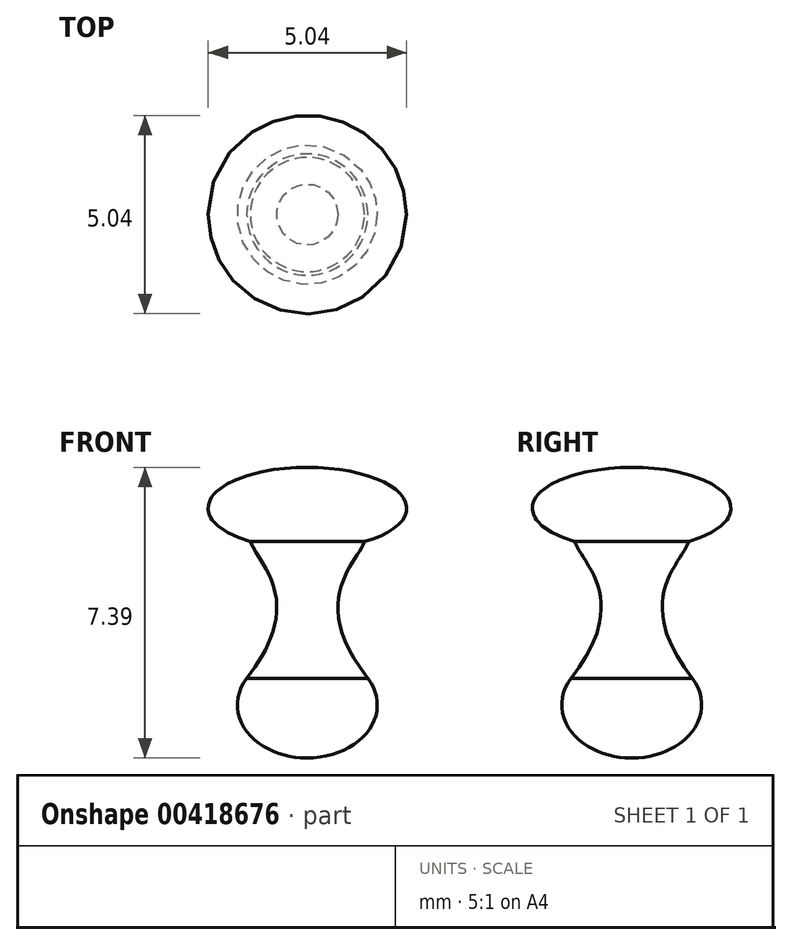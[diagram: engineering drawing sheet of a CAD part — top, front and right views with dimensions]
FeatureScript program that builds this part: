
annotation { "Feature Type Name" : "Feature", "Feature Type Description" : "" }
export const myFeature = defineFeature(function(context is Context, id is Id, definition is map)
    precondition{}
    {
        {
            var Q0;
            Q0=qCreatedBy(makeId("Front.planeOp"),FACE);
            var sketch = newSketch(context, id + "F0", { "sketchPlane" : qUnion([Q0])});
            skEllipse(sketch, "E0", {"center": v(0, 5) * mm, "majorRadius": 2.52 * mm, "minorRadius": 1.04 * mm, "majorAxis": v(-1, 0)});
            skEllipse(sketch, "E1", {"center": v(0, 0) * mm, "majorRadius": 1.78 * mm, "minorRadius": 1.35 * mm, "majorAxis": v(1, 0)});
            skLineSegment(sketch, "E2", {"start": v(0, 6.04) * mm, "end": v(0, 3.96) * mm});
            skLineSegment(sketch, "E3", {"start": v(0, 3.96) * mm, "end": v(0, 1.35) * mm});
            skLineSegment(sketch, "E4", {"start": v(0, 1.35) * mm, "end": v(0, -1.35) * mm});
            skFitSpline(sketch, "E5", {"points": [v(1.45, 4.15) * mm, v(1.54, 0.67) * mm], "startDerivative": vector(-0.67, -1.76) * mm, "endDerivative": vector(4.62, -5.94) * mm});
            skSolve(sketch);
        }
        {
            var Q0;
            {var subQ0=sQuery(id+"F0.wireOp",EDGE,"E2");Q0=makeQuery(id+"F0.imprint","IMPRINT",FACE,{"disambiguationData":[TD([[makeQuery(id+"F0.imprint","IMPRINT",EDGE,{"derivedFrom":subQ0}),1.0]])]});}
            var Q1;
            {var subQ0=sQuery(id+"F0.wireOp",EDGE,"E3");Q1=makeQuery(id+"F0.imprint","IMPRINT",FACE,{"disambiguationData":[TD([[makeQuery(id+"F0.imprint","IMPRINT",EDGE,{"derivedFrom":subQ0}),1.0]])]});}
            var Q2;
            {var subQ0=sQuery(id+"F0.wireOp",EDGE,"E4");Q2=makeQuery(id+"F0.imprint","IMPRINT",FACE,{"disambiguationData":[TD([[makeQuery(id+"F0.imprint","IMPRINT",EDGE,{"derivedFrom":subQ0}),1.0]])]});}
            var Q3;
            Q3=sQuery(id+"F0.wireOp",EDGE,"E3");
            revolve(context, id + "F1", {"surfaceOperationType" : NewSurfaceOperationType.NEW, "entities" : qUnion([Q0, Q1, Q2]), "axis" : qUnion([Q3]), "revolveType" : RevolveType.FULL});
        }
    });
